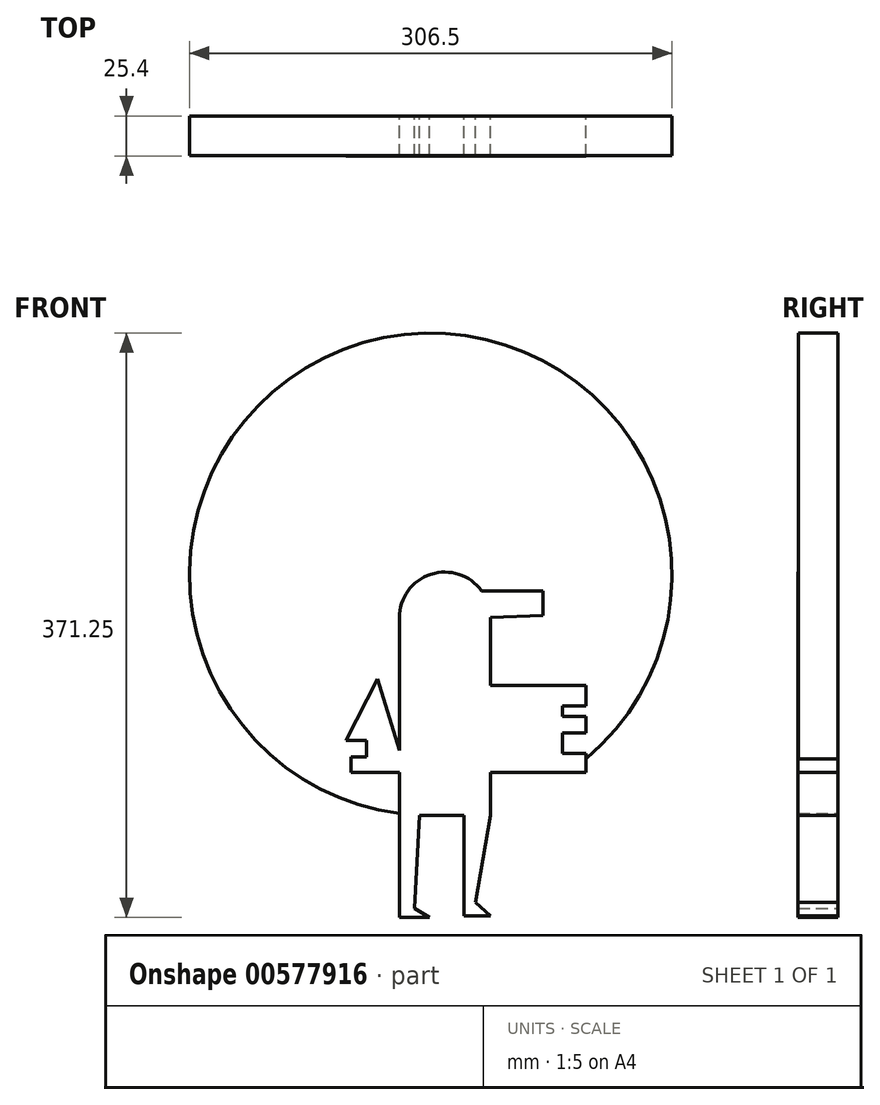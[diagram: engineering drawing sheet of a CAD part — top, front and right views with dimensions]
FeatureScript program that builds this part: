
annotation { "Feature Type Name" : "Feature", "Feature Type Description" : "" }
export const myFeature = defineFeature(function(context is Context, id is Id, definition is map)
    precondition{}
    {
        {
            var Q0;
            Q0=qCreatedBy(makeId("Front.planeOp"),FACE);
            var sketch = newSketch(context, id + "F0", { "sketchPlane" : qUnion([Q0])});
            skLineSegment(sketch, "E0.bottom", {"start": v(28.87, 62.8) * mm, "end": v(-28.87, 62.8) * mm});
            skLineSegment(sketch, "E0.top", {"start": v(28.87, -62.8) * mm, "end": v(-28.87, -62.8) * mm});
            skLineSegment(sketch, "E0.left", {"start": v(28.87, 62.8) * mm, "end": v(28.87, -62.8) * mm});
            skLineSegment(sketch, "E0.right", {"start": v(-28.87, 62.8) * mm, "end": v(-28.87, -62.8) * mm});
            skPoint(sketch, "E0.middle", {"position": v(0, 0) * mm});
            skLineSegment(sketch, "E1", {"start": v(-28.87, -62.8) * mm, "end": v(-28.87, -115.85) * mm});
            skLineSegment(sketch, "E2", {"start": v(-28.87, -115.85) * mm, "end": v(-9.74, -127.75) * mm});
            skLineSegment(sketch, "E3", {"start": v(-9.74, -127.75) * mm, "end": v(-28.87, -127.75) * mm});
            skLineSegment(sketch, "E4", {"start": v(-28.87, -127.75) * mm, "end": v(-28.87, -115.85) * mm});
            skLineSegment(sketch, "E5", {"start": v(-16.24, -62.8) * mm, "end": v(-19.3, -121.8) * mm});
            skLineSegment(sketch, "E6", {"start": v(12.05, -62.8) * mm, "end": v(12.05, -126.8) * mm});
            skLineSegment(sketch, "E7", {"start": v(12.05, -126.8) * mm, "end": v(28.87, -126.8) * mm});
            skLineSegment(sketch, "E8", {"start": v(28.87, -126.8) * mm, "end": v(19.58, -118.16) * mm});
            skLineSegment(sketch, "E9", {"start": v(19.58, -118.16) * mm, "end": v(28.87, -62.8) * mm});
            skLineSegment(sketch, "E10", {"start": v(28.87, 19.73) * mm, "end": v(74.5, 19.73) * mm});
            skLineSegment(sketch, "E11", {"start": v(74.5, 19.73) * mm, "end": v(89.72, 19.73) * mm});
            skLineSegment(sketch, "E12", {"start": v(89.72, 19.73) * mm, "end": v(89.72, 6.52) * mm});
            skLineSegment(sketch, "E13", {"start": v(89.72, 6.52) * mm, "end": v(74.83, 6.52) * mm});
            skLineSegment(sketch, "E14", {"start": v(74.83, 6.52) * mm, "end": v(74.83, 0) * mm});
            skLineSegment(sketch, "E15", {"start": v(74.83, 0) * mm, "end": v(89.72, 0) * mm});
            skLineSegment(sketch, "E16", {"start": v(89.72, 0) * mm, "end": v(89.72, -10.44) * mm});
            skLineSegment(sketch, "E17", {"start": v(89.72, -10.44) * mm, "end": v(74.83, -10.44) * mm});
            skLineSegment(sketch, "E18", {"start": v(74.83, -10.44) * mm, "end": v(74.83, -23.4) * mm});
            skLineSegment(sketch, "E19", {"start": v(74.83, -23.4) * mm, "end": v(89.72, -23.4) * mm});
            skLineSegment(sketch, "E20", {"start": v(89.72, -23.4) * mm, "end": v(89.72, -35.69) * mm});
            skLineSegment(sketch, "E21", {"start": v(89.72, -35.69) * mm, "end": v(28.87, -35.69) * mm});
            skLineSegment(sketch, "E22", {"start": v(28.87, -35.69) * mm, "end": v(-59.58, -35.69) * mm});
            skLineSegment(sketch, "E23", {"start": v(-59.58, -35.69) * mm, "end": v(-59.58, -25.67) * mm});
            skLineSegment(sketch, "E24", {"start": v(-59.58, -25.67) * mm, "end": v(-49.64, -25.67) * mm});
            skLineSegment(sketch, "E25", {"start": v(-49.64, -25.67) * mm, "end": v(-49.64, -15.2) * mm});
            skLineSegment(sketch, "E26", {"start": v(-49.64, -15.2) * mm, "end": v(-62.85, -15.2) * mm});
            skLineSegment(sketch, "E27", {"start": v(-62.85, -15.2) * mm, "end": v(-42.67, 23.78) * mm});
            skLineSegment(sketch, "E28", {"start": v(-42.67, 23.78) * mm, "end": v(-28.87, -21.68) * mm});
            skArc(sketch, "E29", {"start": v(28.87, 62.8) * mm, "mid": v(0, 91.67) * mm, "end": v(-28.87, 62.8) * mm});
            skLineSegment(sketch, "E30", {"start": v(23.33, 79.8) * mm, "end": v(62.25, 79.8) * mm});
            skLineSegment(sketch, "E31", {"start": v(62.25, 79.8) * mm, "end": v(62.25, 64.1) * mm});
            skLineSegment(sketch, "E32", {"start": v(62.25, 64.1) * mm, "end": v(28.87, 62.8) * mm});
            skSolve(sketch);
        }
        {
            var Q0;
            Q0 = qSketchRegion(id + "F0", true);
            var Q1;
            {var subQ0=sQuery(id+"F0.wireOp",EDGE,"E0.bottom");Q1=makeQuery(id+"F0.imprint","IMPRINT",FACE,{"disambiguationData":[TD([[makeQuery(id+"F0.imprint","IMPRINT",EDGE,{"derivedFrom":subQ0}),-1.0]])]});}
            extrude(context, id + "F1", {"entities" : qUnion([Q0, Q1]), "depth" : 25.4 * mm, "offsetDistance" : 25.4 * mm});
        }
        {
            var Q0;
            Q0=makeQuery(id+"F1.opExtrude","CAP_FACE",FACE,{"disambiguationData":[OSD([sQuery(id+"F0.wireOp",EDGE,"E0.top"),sQuery(id+"F0.wireOp",EDGE,"E0.left"),sQuery(id+"F0.wireOp",EDGE,"E0.right"),sQuery(id+"F0.wireOp",EDGE,"E1"),sQuery(id+"F0.wireOp",EDGE,"E2"),sQuery(id+"F0.wireOp",EDGE,"E3"),sQuery(id+"F0.wireOp",EDGE,"E4"),sQuery(id+"F0.wireOp",EDGE,"E5"),sQuery(id+"F0.wireOp",EDGE,"E6"),sQuery(id+"F0.wireOp",EDGE,"E7"),sQuery(id+"F0.wireOp",EDGE,"E8"),sQuery(id+"F0.wireOp",EDGE,"E9"),sQuery(id+"F0.wireOp",EDGE,"E10"),sQuery(id+"F0.wireOp",EDGE,"E11"),sQuery(id+"F0.wireOp",EDGE,"E12"),sQuery(id+"F0.wireOp",EDGE,"E13"),sQuery(id+"F0.wireOp",EDGE,"E14"),sQuery(id+"F0.wireOp",EDGE,"E15"),sQuery(id+"F0.wireOp",EDGE,"E16"),sQuery(id+"F0.wireOp",EDGE,"E17"),sQuery(id+"F0.wireOp",EDGE,"E18"),sQuery(id+"F0.wireOp",EDGE,"E19"),sQuery(id+"F0.wireOp",EDGE,"E20"),sQuery(id+"F0.wireOp",EDGE,"E21"),sQuery(id+"F0.wireOp",EDGE,"E22"),sQuery(id+"F0.wireOp",EDGE,"E23"),sQuery(id+"F0.wireOp",EDGE,"E24"),sQuery(id+"F0.wireOp",EDGE,"E25"),sQuery(id+"F0.wireOp",EDGE,"E26"),sQuery(id+"F0.wireOp",EDGE,"E27"),sQuery(id+"F0.wireOp",EDGE,"E28"),sQuery(id+"F0.wireOp",EDGE,"E29"),sQuery(id+"F0.wireOp",EDGE,"E30"),sQuery(id+"F0.wireOp",EDGE,"E31"),sQuery(id+"F0.wireOp",EDGE,"E32")])],"isStart":true});
            var sketch = newSketch(context, id + "F2", { "sketchPlane" : qUnion([Q0])});
            skCircle(sketch, "E33", {"center": v(8.94, 90.25) * mm, "radius": 153.25 * mm});
            skSolve(sketch);
        }
        {
            var Q0;
            {var subQ4=sQuery(id+"F0.wireOp",EDGE,"E0.right");Q0=makeQuery(id+"F2.imprint","IMPRINT",FACE,{"disambiguationData":[TD([[makeQuery(id+"F2.imprint","IMPRINT",EDGE,{"derivedFrom":makeQuery(id+"F1.opExtrude","CAP_EDGE",EDGE,{"disambiguationData":[OSD([subQ4])],"isStart":true})}),1.0]])]});}
            extrude(context, id + "F3", {"entities" : qUnion([Q0]), "operationType" : NewBodyOperationType.ADD, "oppositeDirection" : true, "depth" : 25.26 * mm, "offsetDistance" : 25.4 * mm});
        }
    });
